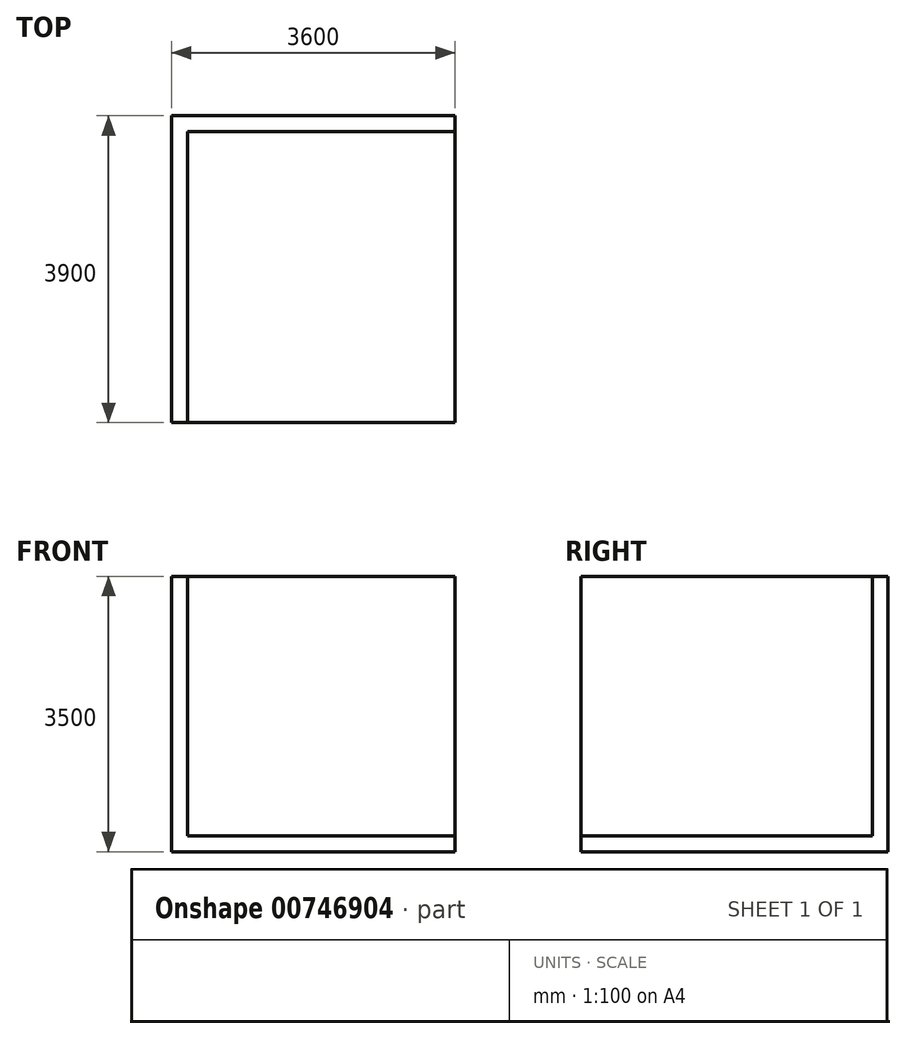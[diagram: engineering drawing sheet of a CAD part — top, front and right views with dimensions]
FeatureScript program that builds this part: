
annotation { "Feature Type Name" : "Feature", "Feature Type Description" : "" }
export const myFeature = defineFeature(function(context is Context, id is Id, definition is map)
    precondition{}
    {
        {
            var Q0;
            Q0=qCreatedBy(makeId("Top.planeOp"),FACE);
            var sketch = newSketch(context, id + "F0", { "sketchPlane" : qUnion([Q0])});
            skLineSegment(sketch, "E0.bottom", {"start": v(1800, -1950) * mm, "end": v(-1800, -1950) * mm});
            skLineSegment(sketch, "E0.top", {"start": v(1800, 1950) * mm, "end": v(-1800, 1950) * mm});
            skLineSegment(sketch, "E0.left", {"start": v(1800, -1950) * mm, "end": v(1800, 1950) * mm});
            skLineSegment(sketch, "E0.right", {"start": v(-1800, -1950) * mm, "end": v(-1800, 1950) * mm});
            skPoint(sketch, "E0.middle", {"position": v(0, 0) * mm});
            skSolve(sketch);
        }
        {
            var Q0;
            Q0 = qSketchRegion(id + "F0", true);
            extrude(context, id + "F1", {"entities" : qUnion([Q0]), "depth" : 3500 * mm, "offsetDistance" : 25 * mm});
        }
        {
            var Q0;
            Q0=makeQuery(id+"F1.opExtrude","CAP_FACE",FACE,{"disambiguationData":[OSD([sQuery(id+"F0.wireOp",EDGE,"E0.bottom"),sQuery(id+"F0.wireOp",EDGE,"E0.top"),sQuery(id+"F0.wireOp",EDGE,"E0.left"),sQuery(id+"F0.wireOp",EDGE,"E0.right")])],"isStart":false});
            var Q1;
            Q1=makeQuery(id+"F1.opExtrude","SWEPT_FACE",FACE,{"disambiguationData":[OSD([sQuery(id+"F0.wireOp",EDGE,"E0.left")])]});
            var Q2;
            Q2=makeQuery(id+"F1.opExtrude","SWEPT_FACE",FACE,{"disambiguationData":[OSD([sQuery(id+"F0.wireOp",EDGE,"E0.bottom")])]});
            shell(context, id + "F2", {"entities" : qUnion([Q0, Q1, Q2]), "thickness" : 200 * mm});
        }
    });
